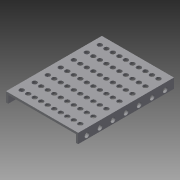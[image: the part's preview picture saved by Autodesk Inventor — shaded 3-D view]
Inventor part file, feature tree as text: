
AUTODESK INVENTOR PART (.ipt)
format: ipt  version: 2015 (Build 190159000, 159)  size: 325,632 bytes
history: native  units: in
note: dims shown in document units (in); Inventor stores cm internally (conversion verified against a paired STEP export)
features: extrude x12, sketch x12, pattern_linear x5
ambient origin geometry x8: Origin, YZ Plane, XZ Plane, XY Plane, X Axis, Y Axis, Z Axis, Center Point
bodies: Solid1 (feature_tree)
feature tree (29):
  extrude  "Extrusion1"  Depth=3.4744in
  extrude  "Extrusion2"  Depth=0.0787in
  pattern_linear  "Rectangular Pattern1"  Count1=15 Spacing1=0.2362in
  extrude  "Extrusion3"  Depth=0.122in TaperAngle=0.0deg
  extrude  "Extrusion4"  Depth=0.0787in
  extrude  "Extrusion5"  Depth=0.0787in
  extrude  "Extrusion6"  Depth=0.2756in
  extrude  "Extrusion7"  Depth=0.0837in
  pattern_linear  "Rectangular Pattern2"  Count1=15 Spacing1=0.2362in
  extrude  "Extrusion8"  Depth=0.0787in TaperAngle=0.0deg
  pattern_linear  "Rectangular Pattern3"  Count1=9 Spacing1=0.4724in
  extrude  "Extrusion9"  Depth=0.0787in
  extrude  "Extrusion10"  Depth=0.0787in TaperAngle=0.0deg
  pattern_linear  "Rectangular Pattern4"  Spacing1=0.1673in  [1 undecoded]
  extrude  "Extrusion11"  Depth=0.0787in TaperAngle=0.0deg
  pattern_linear  "Rectangular Pattern5"  Count1=9 Spacing1=0.4724in
  extrude  "Extrusion12"  Depth=0.0787in
  sketch  "Sketch1"  dims[d0=2.4508in d1=3.4744in]
  sketch  "Sketch2"  dims[d2=0.0787in d3=0.0in d4=0.0074in]
  sketch  "Sketch3"  dims[d7=0.1673in]
  sketch  "Sketch4"  dims[d8=0.0787in d9=0.0in d10=5.9055in d12=0.2362in]
  sketch  "Sketch5"  dims[d13=3.937in d15=0.2362in d16=0.122in d17=0.0in]
  sketch  "Sketch6"  dims[d18=0.0433in d19=0.0in d20=0.0787in]
  sketch  "Sketch7"  dims[d21=0.2756in d22=0.0in d23=0.0787in]
  sketch  "Sketch8"  dims[d24=0.2756in d25=0.0in d26=0.0344in]
  sketch  "Sketch9"  dims[d27=0.0837in d28=0.0837in]
  sketch  "Sketch10"  dims[d29=0.1673in]
  sketch  "Sketch11"  dims[d30=0.2756in d31=0.0in d32=5.9055in d34=0.2362in]
  sketch  "Sketch12"  dims[d36=0.1673in d37=0.0787in d38=0.0in d39=3.5433in d41=0.4724in d42=3.937in d44=0.2362in d45=0.0787in d46=0.0in d48=0.1673in d49=0.0787in d50=0.0in d51=3.5433in d53=0.4724in d55=0.1673in d56=0.0787in d57=0.0in d58=3.5433in d60=0.4724in d61=0.0787in d62=0.0in]
note: 1 required parameter value undecoded (feature->parameter linkage not recoverable at this tier; creation-order binding heuristic only, values carry confidence <= 0.55)
